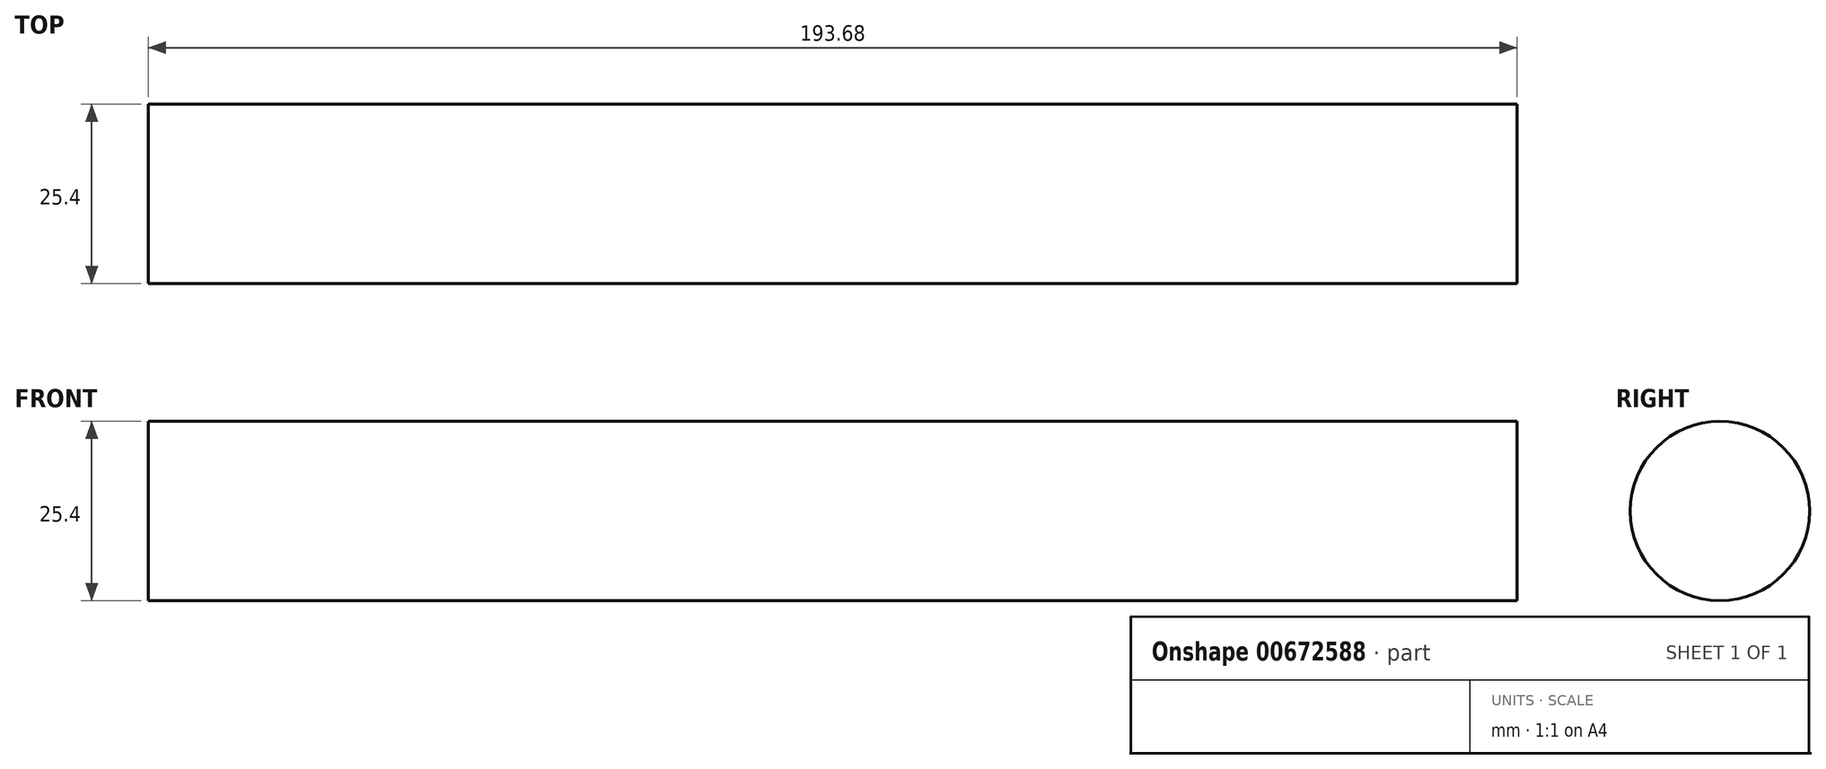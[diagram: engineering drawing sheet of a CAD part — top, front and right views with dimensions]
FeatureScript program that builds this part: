
annotation { "Feature Type Name" : "Feature", "Feature Type Description" : "" }
export const myFeature = defineFeature(function(context is Context, id is Id, definition is map)
    precondition{}
    {
        {
            var Q0;
            Q0=qCreatedBy(makeId("Right.planeOp"),FACE);
            var sketch = newSketch(context, id + "F0", { "sketchPlane" : qUnion([Q0])});
            skCircle(sketch, "E0", {"center": v(0, 0) * mm, "radius": 12.7 * mm});
            skSolve(sketch);
        }
        {
            var Q0;
            Q0=qSketchRegion(id+"F0",true);
            extrude(context, id + "F1", {"entities" : qUnion([Q0]), "depth" : 193.67 * mm, "offsetDistance" : 25.4 * mm});
        }
    });
